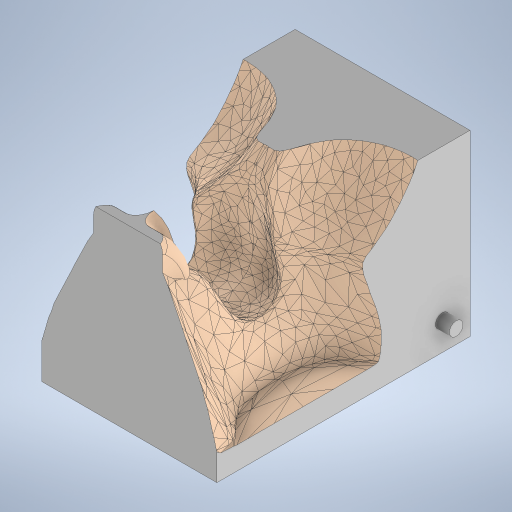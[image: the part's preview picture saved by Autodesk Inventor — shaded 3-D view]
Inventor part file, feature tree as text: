
AUTODESK INVENTOR PART (.ipt)
format: ipt  version: 2024 (Build 280153000, 153)  size: 11,120,640 bytes
history: native  units: mm
features: other x6, sketch x5, extrude x4, plane x2
ambient origin geometry x8: Origin, YZ Plane, XZ Plane, XY Plane, X Axis, Y Axis, Z Axis, Center Point
bodies: Body1 (feature_tree)
feature tree (17):
  other  "M.ipt"
  plane  "Plano de trabajo1"
  extrude  "Extrusión1"  [1 undecoded]
  other  "Combinar1"
  sketch  "Boceto3"  dims[d2=550.0mm d3=520.0mm]
  sketch  "Boceto4"  dims[d4=550.0mm d5=0.0mm d6=129.8482mm]
  plane  "Plano de trabajo2"
  sketch  "Boceto5"  dims[d17=180.0mm d18=180.0mm]
  extrude  "Extrusión2"  Depth=520.0mm
  extrude  "Extrusión3"  Depth=129.8482mm
  extrude  "Extrusión4"  Depth=180.0mm
  other  "Sólido1::M.ipt"
  other  "OperaciónIdentificador1"
  sketch  "Boceto1"  dims[d0=25.0mm d1=-365.0mm]
  other  "Sólido2"
  sketch  "Boceto6"  dims[d22=326.0mm d23=180.0mm d24=180.0mm d25=180.0mm d26=10.0mm d27=0.0mm d28=1000.0mm d29=0.0mm d30=30.0mm d31=30.0mm d32=15.0mm d33=15.0mm d34=205.0mm d35=0.0mm d36=0.0mm d14=0.5mm d15=0.872665mm d16=0.5mm d19=0.5mm d20=0.872665mm d21=0.5mm]
  other  "Sólido1"
note: 1 required parameter value undecoded (feature->parameter linkage not recoverable at this tier; creation-order binding heuristic only, values carry confidence <= 0.55)
